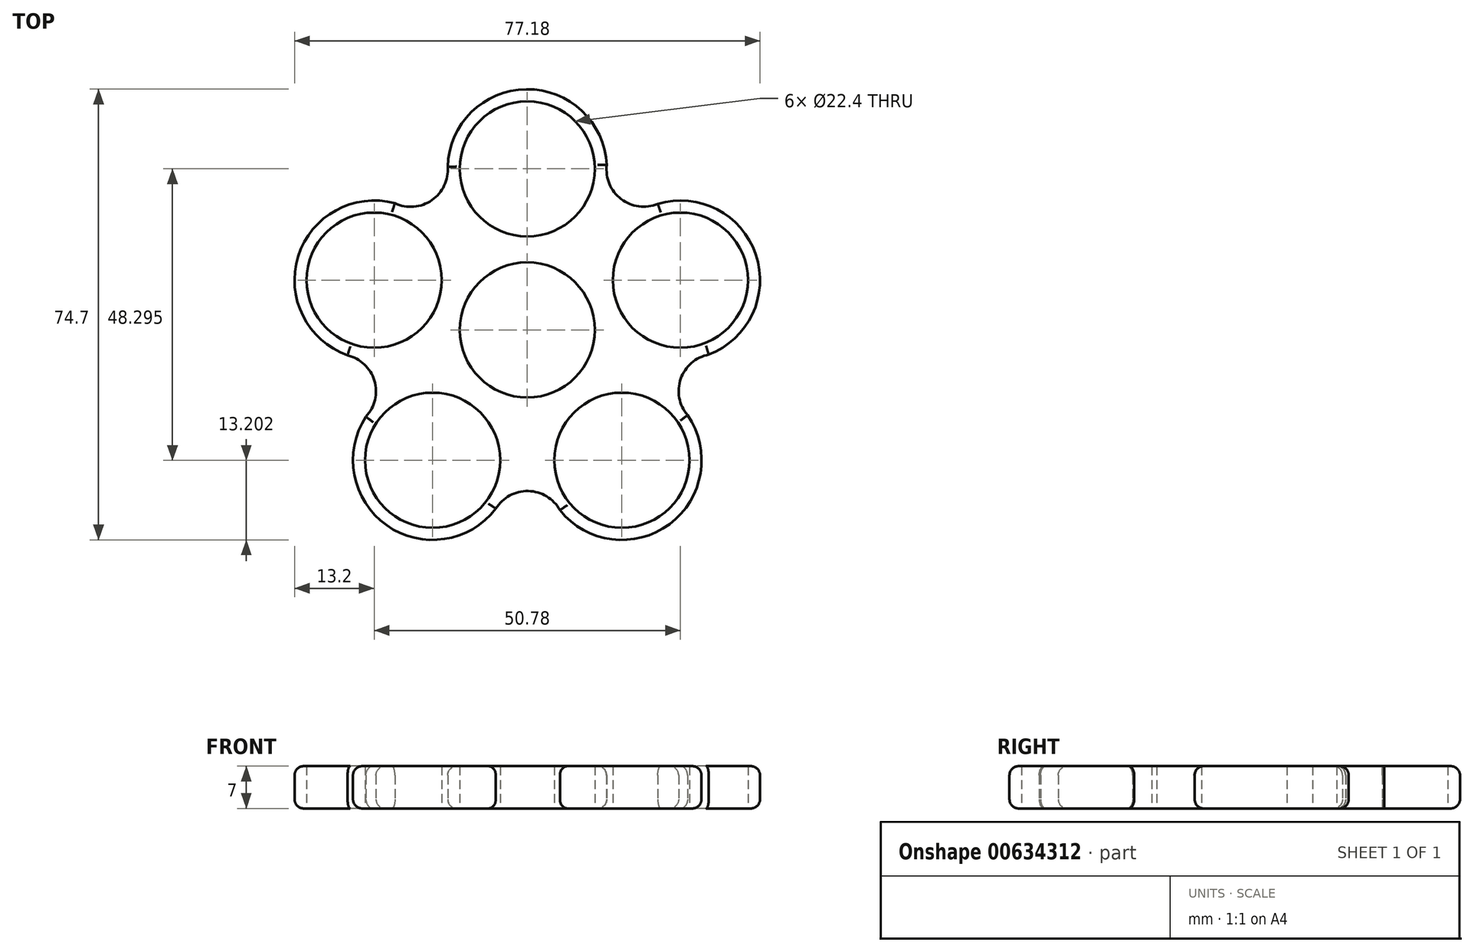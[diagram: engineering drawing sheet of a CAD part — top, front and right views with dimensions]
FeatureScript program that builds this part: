
annotation { "Feature Type Name" : "Feature", "Feature Type Description" : "" }
export const myFeature = defineFeature(function(context is Context, id is Id, definition is map)
    precondition{}
    {
        {
            var Q0;
            Q0=qCreatedBy(makeId("Top.planeOp"),FACE);
            var sketch = newSketch(context, id + "F0", { "sketchPlane" : qUnion([Q0])});
            skCircle(sketch, "E0", {"center": v(0, 0) * mm, "radius": 11.2 * mm});
            skCircle(sketch, "E1", {"center": v(0, 26.7) * mm, "radius": 11.2 * mm});
            skArc(sketch, "E2", {"start": v(13.18, 25.91) * mm, "mid": v(0.13, 39.9) * mm, "end": v(-13.19, 26.18) * mm});
            skCircle(sketch, "E3.1.0", {"center": v(-25.4, 8.25) * mm, "radius": 11.2 * mm});
            skArc(sketch, "E3.1.1", {"start": v(-20.57, 20.54) * mm, "mid": v(-37.9, 12.45) * mm, "end": v(-28.97, -4.45) * mm});
            skCircle(sketch, "E3.2.0", {"center": v(-15.7, -21.6) * mm, "radius": 11.2 * mm});
            skArc(sketch, "E3.2.1", {"start": v(-25.9, -13.22) * mm, "mid": v(-23.56, -32.2) * mm, "end": v(-4.72, -28.93) * mm});
            skCircle(sketch, "E3.3.0", {"center": v(15.7, -21.6) * mm, "radius": 11.2 * mm});
            skArc(sketch, "E3.3.1", {"start": v(4.57, -28.71) * mm, "mid": v(23.34, -32.35) * mm, "end": v(26.06, -13.43) * mm});
            skCircle(sketch, "E3.4.0", {"center": v(25.4, 8.25) * mm, "radius": 11.2 * mm});
            skArc(sketch, "E3.4.1", {"start": v(28.72, -4.52) * mm, "mid": v(37.98, 12.2) * mm, "end": v(20.82, 20.63) * mm});
            skArc(sketch, "E4", {"start": v(13.18, 27.34) * mm, "mid": v(15.57, 21.7) * mm, "end": v(21.64, 20.9) * mm});
            skArc(sketch, "E5.1.0", {"start": v(-21.93, 20.99) * mm, "mid": v(-15.83, 21.5) * mm, "end": v(-13.2, 27.04) * mm});
            skArc(sketch, "E5.2.0", {"start": v(-26.74, -14.37) * mm, "mid": v(-25.35, -8.4) * mm, "end": v(-29.8, -4.2) * mm});
            skArc(sketch, "E5.3.0", {"start": v(5.4, -29.87) * mm, "mid": v(0.16, -26.7) * mm, "end": v(-5.22, -29.63) * mm});
            skArc(sketch, "E5.4.0", {"start": v(30.08, -4.09) * mm, "mid": v(25.45, -8.1) * mm, "end": v(26.57, -14.12) * mm});
            skSolve(sketch);
        }
        {
            var Q0;
            Q0=makeQuery(id+"F0.imprint","IMPRINT",FACE,{"disambiguationData":[TD([[makeQuery(id+"F0.imprint","IMPRINT",EDGE,{"derivedFrom":sQuery(id+"F0.wireOp",EDGE,"E0")}),-1.0]])]});
            extrude(context, id + "F1", {"entities" : qUnion([Q0]), "depth" : 7 * mm, "offsetDistance" : 25 * mm});
        }
        {
            var Q0;
            Q0=makeQuery(id+"F1.opExtrude","CAP_EDGE",EDGE,{"disambiguationData":[OSD([sQuery(id+"F0.wireOp",EDGE,"E3.1.1")])],"isStart":false});
            var Q1;
            Q1=makeQuery(id+"F1.opExtrude","CAP_EDGE",EDGE,{"disambiguationData":[OSD([sQuery(id+"F0.wireOp",EDGE,"E5.2.0")])],"isStart":false});
            var Q2;
            Q2=makeQuery(id+"F1.opExtrude","CAP_EDGE",EDGE,{"disambiguationData":[OSD([sQuery(id+"F0.wireOp",EDGE,"E3.2.1")])],"isStart":false});
            var Q3;
            Q3=makeQuery(id+"F1.opExtrude","CAP_EDGE",EDGE,{"disambiguationData":[OSD([sQuery(id+"F0.wireOp",EDGE,"E5.3.0")])],"isStart":false});
            var Q4;
            Q4=makeQuery(id+"F1.opExtrude","CAP_EDGE",EDGE,{"disambiguationData":[OSD([sQuery(id+"F0.wireOp",EDGE,"E3.3.1")])],"isStart":false});
            var Q5;
            Q5=makeQuery(id+"F1.opExtrude","CAP_EDGE",EDGE,{"disambiguationData":[OSD([sQuery(id+"F0.wireOp",EDGE,"E5.4.0")])],"isStart":false});
            var Q6;
            Q6=makeQuery(id+"F1.opExtrude","CAP_EDGE",EDGE,{"disambiguationData":[OSD([sQuery(id+"F0.wireOp",EDGE,"E3.4.1")])],"isStart":false});
            var Q7;
            Q7=makeQuery(id+"F1.opExtrude","CAP_EDGE",EDGE,{"disambiguationData":[OSD([sQuery(id+"F0.wireOp",EDGE,"E4")])],"isStart":false});
            var Q8;
            Q8=makeQuery(id+"F1.opExtrude","CAP_EDGE",EDGE,{"disambiguationData":[OSD([sQuery(id+"F0.wireOp",EDGE,"E2")])],"isStart":false});
            var Q9;
            Q9=makeQuery(id+"F1.opExtrude","CAP_EDGE",EDGE,{"disambiguationData":[OSD([sQuery(id+"F0.wireOp",EDGE,"E5.1.0")])],"isStart":false});
            var Q10;
            Q10=makeQuery(id+"F1.opExtrude","CAP_EDGE",EDGE,{"disambiguationData":[OSD([sQuery(id+"F0.wireOp",EDGE,"E3.2.1")])],"isStart":true});
            var Q11;
            Q11=makeQuery(id+"F1.opExtrude","CAP_EDGE",EDGE,{"disambiguationData":[OSD([sQuery(id+"F0.wireOp",EDGE,"E5.3.0")])],"isStart":true});
            var Q12;
            Q12=makeQuery(id+"F1.opExtrude","CAP_EDGE",EDGE,{"disambiguationData":[OSD([sQuery(id+"F0.wireOp",EDGE,"E3.3.1")])],"isStart":true});
            var Q13;
            Q13=makeQuery(id+"F1.opExtrude","CAP_EDGE",EDGE,{"disambiguationData":[OSD([sQuery(id+"F0.wireOp",EDGE,"E5.4.0")])],"isStart":true});
            var Q14;
            Q14=makeQuery(id+"F1.opExtrude","CAP_EDGE",EDGE,{"disambiguationData":[OSD([sQuery(id+"F0.wireOp",EDGE,"E3.4.1")])],"isStart":true});
            var Q15;
            Q15=makeQuery(id+"F1.opExtrude","CAP_EDGE",EDGE,{"disambiguationData":[OSD([sQuery(id+"F0.wireOp",EDGE,"E5.2.0")])],"isStart":true});
            var Q16;
            Q16=makeQuery(id+"F1.opExtrude","CAP_EDGE",EDGE,{"disambiguationData":[OSD([sQuery(id+"F0.wireOp",EDGE,"E3.1.1")])],"isStart":true});
            var Q17;
            Q17=makeQuery(id+"F1.opExtrude","CAP_EDGE",EDGE,{"disambiguationData":[OSD([sQuery(id+"F0.wireOp",EDGE,"E4")])],"isStart":true});
            var Q18;
            Q18=makeQuery(id+"F1.opExtrude","CAP_EDGE",EDGE,{"disambiguationData":[OSD([sQuery(id+"F0.wireOp",EDGE,"E2")])],"isStart":true});
            var Q19;
            Q19=makeQuery(id+"F1.opExtrude","CAP_EDGE",EDGE,{"disambiguationData":[OSD([sQuery(id+"F0.wireOp",EDGE,"E5.1.0")])],"isStart":true});
            fillet(context, id + "F2", {"entities" : qUnion([Q0, Q1, Q2, Q3, Q4, Q5, Q6, Q7, Q8, Q9, Q10, Q11, Q12, Q13, Q14, Q15, Q16, Q17, Q18, Q19]), "radius" : 1.5 * mm, "tangentPropagation" : true, "allowEdgeOverflow" : false});
        }
    });
